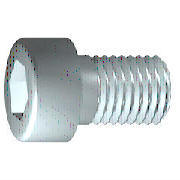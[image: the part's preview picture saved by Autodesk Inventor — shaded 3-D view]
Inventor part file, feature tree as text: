
AUTODESK INVENTOR PART (.ipt)
format: ipt  version: 2017 (Build 210142000, 142)  size: 188,928 bytes
history: native  units: mm (DEFAULTED — no unit token found)
features: sketch x2, other x1, extrude x1, plane x1, fillet x1
ambient origin geometry x7: Origin, YZ Plane, XY Plane, X Axis, Y Axis, Z Axis, Center Point
bodies: Solid1 (feature_tree)
feature tree (6):
  other  "Corps"
  extrude  "Rainure"  Depth=14.75mm
  plane  "Work Plane1"
  fillet  "Fillet2"  Radius=0.306825mm
  sketch  "Esquisse1"
  sketch  "Esquisse2"
